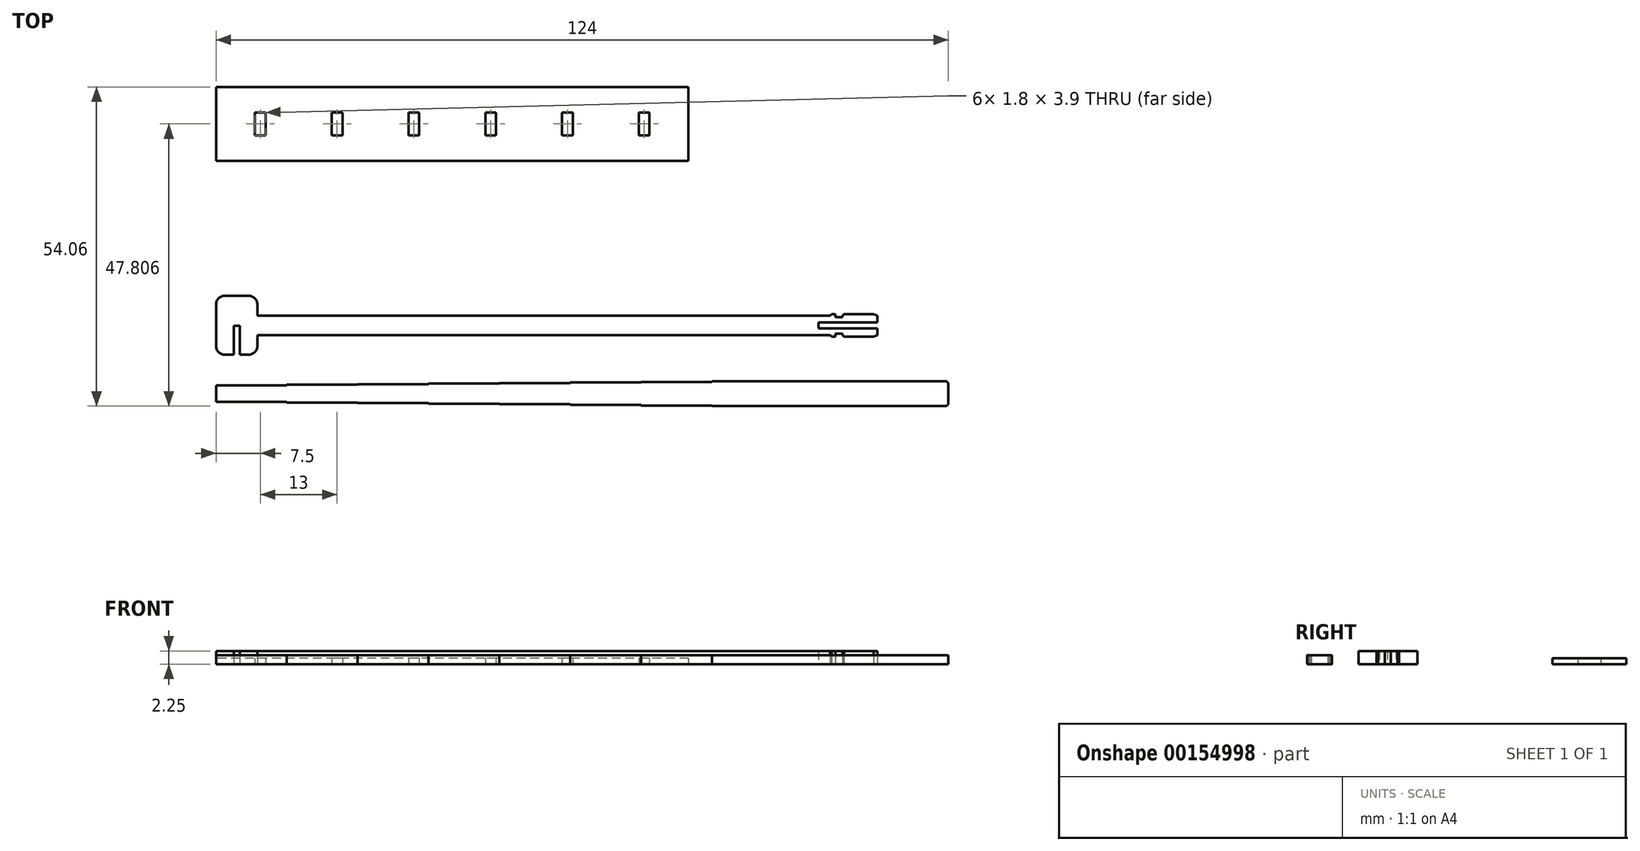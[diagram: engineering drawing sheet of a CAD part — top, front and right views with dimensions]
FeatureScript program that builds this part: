
annotation { "Feature Type Name" : "Feature", "Feature Type Description" : "" }
export const myFeature = defineFeature(function(context is Context, id is Id, definition is map)
    precondition{}
    {
        {
            var Q0;
            Q0=qCreatedBy(makeId("Top.planeOp"),FACE);
            var sketch = newSketch(context, id + "F0", { "sketchPlane" : qUnion([Q0])});
            skLineSegment(sketch, "E0", {"start": v(0, 0) * mm, "end": v(0, -1.4) * mm});
            skLineSegment(sketch, "E1", {"start": v(0, -1.4) * mm, "end": v(12, -1.4) * mm});
            skLineSegment(sketch, "E2", {"start": v(12, -1.4) * mm, "end": v(12, -1.5) * mm});
            skLineSegment(sketch, "E3", {"start": v(12, -1.5) * mm, "end": v(24, -1.5) * mm});
            skLineSegment(sketch, "E4", {"start": v(24, -1.5) * mm, "end": v(24, -1.6) * mm});
            skLineSegment(sketch, "E5", {"start": v(24, -1.6) * mm, "end": v(36, -1.6) * mm});
            skLineSegment(sketch, "E6", {"start": v(36, -1.6) * mm, "end": v(36, -1.7) * mm});
            skLineSegment(sketch, "E7", {"start": v(36, -1.7) * mm, "end": v(48, -1.7) * mm});
            skLineSegment(sketch, "E8", {"start": v(48, -1.7) * mm, "end": v(48, -1.8) * mm});
            skLineSegment(sketch, "E9", {"start": v(48, -1.8) * mm, "end": v(60, -1.8) * mm});
            skLineSegment(sketch, "E10", {"start": v(60, -1.8) * mm, "end": v(60, -1.9) * mm});
            skLineSegment(sketch, "E11", {"start": v(60, -1.9) * mm, "end": v(72, -1.9) * mm});
            skLineSegment(sketch, "E12", {"start": v(72, -1.9) * mm, "end": v(72, -2) * mm});
            skLineSegment(sketch, "E13", {"start": v(72, -2) * mm, "end": v(84, -2) * mm});
            skLineSegment(sketch, "E14", {"start": v(84, -2) * mm, "end": v(84, -2.1) * mm});
            skLineSegment(sketch, "E15", {"start": v(84, -2.1) * mm, "end": v(123.5, -2.1) * mm});
            skLineSegment(sketch, "E16", {"start": v(124, -1.6) * mm, "end": v(124, 0) * mm});
            skLineSegment(sketch, "E17.0", {"start": v(86, -1.1) * mm, "end": v(123, -1.1) * mm});
            skLineSegment(sketch, "E17.2", {"start": v(73, -1) * mm, "end": v(85, -1) * mm});
            skLineSegment(sketch, "E17.3", {"start": v(73, -0.9) * mm, "end": v(73, -1) * mm});
            skLineSegment(sketch, "E17.4", {"start": v(62, -0.9) * mm, "end": v(73, -0.9) * mm});
            skLineSegment(sketch, "E17.5", {"start": v(123, -1.1) * mm, "end": v(123, -0.95) * mm});
            skLineSegment(sketch, "E17.7", {"start": v(49, -0.8) * mm, "end": v(61, -0.8) * mm});
            skLineSegment(sketch, "E17.12", {"start": v(4, -0.5) * mm, "end": v(25, -0.5) * mm});
            skLineSegment(sketch, "E17.13", {"start": v(25, -0.5) * mm, "end": v(25, -0.6) * mm});
            skLineSegment(sketch, "E17.14", {"start": v(16, -0.6) * mm, "end": v(25, -0.6) * mm});
            skLineSegment(sketch, "E17.16", {"start": v(17, -0.7) * mm, "end": v(49, -0.7) * mm});
            skLineSegment(sketch, "E17.17", {"start": v(49, -0.7) * mm, "end": v(49, -0.8) * mm});
            skLineSegment(sketch, "E18", {"start": v(123, -0.95) * mm, "end": v(123, -0.45) * mm});
            skLineSegment(sketch, "E19.MirrorCS", {"start": v(84, 2) * mm, "end": v(84, 2.1) * mm});
            skLineSegment(sketch, "E20.MirrorCS", {"start": v(12, 1.4) * mm, "end": v(12, 1.5) * mm});
            skLineSegment(sketch, "E21.MirrorCS", {"start": v(24, 1.5) * mm, "end": v(24, 1.6) * mm});
            skLineSegment(sketch, "E22.MirrorCS", {"start": v(123, 0.95) * mm, "end": v(123, 0.45) * mm});
            skLineSegment(sketch, "E23.MirrorCS", {"start": v(48, 1.7) * mm, "end": v(48, 1.8) * mm});
            skLineSegment(sketch, "E24.MirrorCS", {"start": v(49, 0.7) * mm, "end": v(49, 0.8) * mm});
            skLineSegment(sketch, "E25.MirrorCS", {"start": v(73, 0.9) * mm, "end": v(73, 1) * mm});
            skLineSegment(sketch, "E26.MirrorCS", {"start": v(72, 1.9) * mm, "end": v(72, 2) * mm});
            skLineSegment(sketch, "E27.MirrorCS", {"start": v(60, 1.8) * mm, "end": v(60, 1.9) * mm});
            skLineSegment(sketch, "E28.MirrorCS", {"start": v(25, 0.5) * mm, "end": v(25, 0.6) * mm});
            skLineSegment(sketch, "E29.MirrorCS", {"start": v(36, 1.6) * mm, "end": v(36, 1.7) * mm});
            skLineSegment(sketch, "E30.MirrorCS", {"start": v(84, 2.1) * mm, "end": v(123.5, 2.1) * mm});
            skLineSegment(sketch, "E31.MirrorCS", {"start": v(0, 0) * mm, "end": v(0, 1.4) * mm});
            skLineSegment(sketch, "E32.MirrorCS", {"start": v(0, 1.4) * mm, "end": v(12, 1.4) * mm});
            skLineSegment(sketch, "E33.MirrorCS", {"start": v(12, 1.5) * mm, "end": v(24, 1.5) * mm});
            skLineSegment(sketch, "E34.MirrorCS", {"start": v(24, 1.6) * mm, "end": v(36, 1.6) * mm});
            skLineSegment(sketch, "E35.MirrorCS", {"start": v(86, 1.1) * mm, "end": v(123, 1.1) * mm});
            skLineSegment(sketch, "E36.MirrorCS", {"start": v(124, 1.6) * mm, "end": v(124, 0) * mm});
            skLineSegment(sketch, "E37.MirrorCS", {"start": v(48, 1.8) * mm, "end": v(60, 1.8) * mm});
            skLineSegment(sketch, "E38.MirrorCS", {"start": v(60, 1.9) * mm, "end": v(72, 1.9) * mm});
            skLineSegment(sketch, "E39.MirrorCS", {"start": v(4, 0.5) * mm, "end": v(25, 0.5) * mm});
            skLineSegment(sketch, "E40.MirrorCS", {"start": v(16, 0.6) * mm, "end": v(25, 0.6) * mm});
            skLineSegment(sketch, "E41.MirrorCS", {"start": v(17, 0.7) * mm, "end": v(49, 0.7) * mm});
            skLineSegment(sketch, "E42.MirrorCS", {"start": v(62, 0.9) * mm, "end": v(73, 0.9) * mm});
            skLineSegment(sketch, "E43.MirrorCS", {"start": v(49, 0.8) * mm, "end": v(61, 0.8) * mm});
            skLineSegment(sketch, "E44.MirrorCS", {"start": v(72, 2) * mm, "end": v(84, 2) * mm});
            skLineSegment(sketch, "E45.MirrorCS", {"start": v(73, 1) * mm, "end": v(85, 1) * mm});
            skLineSegment(sketch, "E46.MirrorCS", {"start": v(36, 1.7) * mm, "end": v(48, 1.7) * mm});
            skLineSegment(sketch, "E47.MirrorCS", {"start": v(123, 1.1) * mm, "end": v(123, 0.95) * mm});
            skLineSegment(sketch, "E48", {"start": v(16, 0.6) * mm, "end": v(16, -0.6) * mm});
            skLineSegment(sketch, "E49", {"start": v(17, -0.7) * mm, "end": v(17, 0.7) * mm});
            skLineSegment(sketch, "E50", {"start": v(61, -0.8) * mm, "end": v(61, 0.8) * mm});
            skLineSegment(sketch, "E51", {"start": v(86, -1.1) * mm, "end": v(86, 1.1) * mm});
            skPoint(sketch, "E52.orphan", {"position": v(37, -0.7) * mm});
            skPoint(sketch, "E53.orphan", {"position": v(61, -0.9) * mm});
            skPoint(sketch, "E54.orphan", {"position": v(85, -1.1) * mm});
            skPoint(sketch, "E55.MirrorCS.end.orphan", {"position": v(85, 1.1) * mm});
            skPoint(sketch, "E56.MirrorCS.end.orphan", {"position": v(61, 0.9) * mm});
            skPoint(sketch, "E57.MirrorCS.end.orphan", {"position": v(37, 0.7) * mm});
            skLineSegment(sketch, "E58.trimOffspring", {"start": v(62, 0.9) * mm, "end": v(62, -0.9) * mm});
            skLineSegment(sketch, "E59", {"start": v(4, -0.5) * mm, "end": v(4, 0.5) * mm});
            skLineSegment(sketch, "E60", {"start": v(123, -0.45) * mm, "end": v(123, 0.45) * mm});
            skLineSegment(sketch, "E61.trimOffspring", {"start": v(85, 1) * mm, "end": v(85, -1) * mm});
            skPoint(sketch, "E62.visualSharp", {"position": v(124, -2.1) * mm});
            skArc(sketch, "E62.filletArc", {"start": v(123.5, -2.1) * mm, "mid": v(123.85, -1.95) * mm, "end": v(124, -1.6) * mm});
            skPoint(sketch, "E63.visualSharp", {"position": v(124, 2.1) * mm});
            skArc(sketch, "E63.filletArc", {"start": v(124, 1.6) * mm, "mid": v(123.85, 1.95) * mm, "end": v(123.5, 2.1) * mm});
            skLineSegment(sketch, "E64", {"start": v(0, 8.08) * mm, "end": v(0, 11.58) * mm});
            skPoint(sketch, "E64.startSnap0", {"position": v(0, 0.7) * mm});
            skLineSegment(sketch, "E65", {"start": v(0, 11.58) * mm, "end": v(102, 11.58) * mm});
            skLineSegment(sketch, "E66", {"start": v(112, 11.08) * mm, "end": v(112, 9.93) * mm});
            skLineSegment(sketch, "E67", {"start": v(5.5, 6.58) * mm, "end": v(4, 6.58) * mm});
            skLineSegment(sketch, "E68", {"start": v(7, 9.93) * mm, "end": v(104, 9.93) * mm});
            skLineSegment(sketch, "E69", {"start": v(7, 9.93) * mm, "end": v(7, 8.08) * mm});
            skLineSegment(sketch, "E70", {"start": v(111.31, 9.68) * mm, "end": v(106.32, 9.68) * mm});
            skPoint(sketch, "E71.orphan", {"position": v(112, 6.58) * mm});
            skLineSegment(sketch, "E72", {"start": v(112, 11.08) * mm, "end": v(102, 11.08) * mm});
            skLineSegment(sketch, "E73", {"start": v(102, 11.08) * mm, "end": v(102, 11.58) * mm});
            skLineSegment(sketch, "E74.MirrorCS", {"start": v(7, 13.23) * mm, "end": v(7, 15.08) * mm});
            skLineSegment(sketch, "E75.MirrorCS", {"start": v(5.5, 16.58) * mm, "end": v(1.5, 16.58) * mm});
            skLineSegment(sketch, "E76.MirrorCS", {"start": v(0, 15.08) * mm, "end": v(0, 11.58) * mm});
            skLineSegment(sketch, "E77.MirrorCS", {"start": v(7, 13.23) * mm, "end": v(104, 13.23) * mm});
            skLineSegment(sketch, "E78.MirrorCS", {"start": v(102, 12.08) * mm, "end": v(102, 11.58) * mm});
            skLineSegment(sketch, "E79.MirrorCS", {"start": v(111.31, 13.48) * mm, "end": v(106.32, 13.48) * mm});
            skLineSegment(sketch, "E80.MirrorCS", {"start": v(112, 12.08) * mm, "end": v(112, 13.23) * mm});
            skLineSegment(sketch, "E81.MirrorCS", {"start": v(112, 12.08) * mm, "end": v(102, 12.08) * mm});
            skPoint(sketch, "E82.MirrorP", {"position": v(112, 16.58) * mm});
            skPoint(sketch, "E83.orphan", {"position": v(112, 11.58) * mm});
            skPoint(sketch, "E84.orphan", {"position": v(112, 13.23) * mm});
            skPoint(sketch, "E85.orphan", {"position": v(112, 9.93) * mm});
            skPoint(sketch, "E86.visualSharp", {"position": v(0, 6.58) * mm});
            skArc(sketch, "E86.filletArc", {"start": v(0, 8.08) * mm, "mid": v(0.44, 7.02) * mm, "end": v(1.5, 6.58) * mm});
            skPoint(sketch, "E87.visualSharp", {"position": v(0, 16.58) * mm});
            skArc(sketch, "E87.filletArc", {"start": v(1.5, 16.58) * mm, "mid": v(0.44, 16.14) * mm, "end": v(0, 15.08) * mm});
            skPoint(sketch, "E88.visualSharp", {"position": v(7, 6.58) * mm});
            skArc(sketch, "E88.filletArc", {"start": v(5.5, 6.58) * mm, "mid": v(6.56, 7.02) * mm, "end": v(7, 8.08) * mm});
            skPoint(sketch, "E89.visualSharp", {"position": v(7, 16.58) * mm});
            skArc(sketch, "E89.filletArc", {"start": v(7, 15.08) * mm, "mid": v(6.56, 16.14) * mm, "end": v(5.5, 16.58) * mm});
            skLineSegment(sketch, "E90", {"start": v(104, 9.93) * mm, "end": v(104.25, 9.68) * mm});
            skLineSegment(sketch, "E91.MirrorCS", {"start": v(104, 13.23) * mm, "end": v(104.25, 13.48) * mm});
            skLineSegment(sketch, "E92", {"start": v(112, 9.93) * mm, "end": v(111.31, 9.68) * mm});
            skLineSegment(sketch, "E93.MirrorCS", {"start": v(112, 13.23) * mm, "end": v(111.31, 13.48) * mm});
            skPoint(sketch, "E94.orphan", {"position": v(104, 9.68) * mm});
            skPoint(sketch, "E95.orphan", {"position": v(104, 13.48) * mm});
            skPoint(sketch, "E96.orphan", {"position": v(112, 9.68) * mm});
            skPoint(sketch, "E97.orphan", {"position": v(112, 13.48) * mm});
            skLineSegment(sketch, "E98", {"start": v(3, 6.58) * mm, "end": v(3, 11.48) * mm});
            skLineSegment(sketch, "E99", {"start": v(3, 11.48) * mm, "end": v(4, 11.48) * mm});
            skLineSegment(sketch, "E100", {"start": v(4, 11.48) * mm, "end": v(4, 6.58) * mm});
            skLineSegment(sketch, "E101.trimOffspring", {"start": v(3, 6.58) * mm, "end": v(1.5, 6.58) * mm});
            skLineSegment(sketch, "E102", {"start": v(107.78, 9.68) * mm, "end": v(107.78, 13.48) * mm, "construction": true});
            skLineSegment(sketch, "E103", {"start": v(104.87, 9.68) * mm, "end": v(104.87, 9.93) * mm});
            skLineSegment(sketch, "E104.0", {"start": v(106.07, 9.68) * mm, "end": v(106.07, 9.93) * mm});
            skLineSegment(sketch, "E105", {"start": v(106.07, 9.93) * mm, "end": v(106.32, 9.68) * mm});
            skLineSegment(sketch, "E106.trimOffspring", {"start": v(104.87, 9.68) * mm, "end": v(104.25, 9.68) * mm});
            skLineSegment(sketch, "E107.MirrorCS", {"start": v(104.87, 13.48) * mm, "end": v(104.87, 13.24) * mm});
            skLineSegment(sketch, "E108.MirrorCS", {"start": v(106.07, 13.24) * mm, "end": v(106.32, 13.48) * mm});
            skLineSegment(sketch, "E109.trimOffspring", {"start": v(104.87, 13.48) * mm, "end": v(104.25, 13.48) * mm});
            skPoint(sketch, "E110.MirrorCS.start.orphan", {"position": v(106.07, 13.48) * mm});
            skLineSegment(sketch, "E111", {"start": v(104.87, 9.93) * mm, "end": v(104.87, 10.18) * mm});
            skLineSegment(sketch, "E112", {"start": v(104.87, 10.18) * mm, "end": v(106.07, 10.18) * mm});
            skLineSegment(sketch, "E113", {"start": v(106.07, 10.18) * mm, "end": v(106.07, 9.93) * mm});
            skLineSegment(sketch, "E114.MirrorCS", {"start": v(104.87, 13.24) * mm, "end": v(104.87, 12.99) * mm});
            skLineSegment(sketch, "E115.MirrorCS", {"start": v(104.87, 12.99) * mm, "end": v(106.07, 12.99) * mm});
            skLineSegment(sketch, "E116.MirrorCS", {"start": v(106.07, 12.99) * mm, "end": v(106.07, 13.24) * mm});
            skSolve(sketch);
        }
        {
            var Q0;
            Q0=makeQuery(id+"F0.imprint","IMPRINT",FACE,{"disambiguationData":[TD([[makeQuery(id+"F0.imprint","IMPRINT",EDGE,{"derivedFrom":sQuery(id+"F0.wireOp",EDGE,"E0")}),1.0]])]});
            var Q1;
            {var subQ0=sQuery(id+"F0.wireOp",EDGE,"E48");var subQ1=sQuery(id+"F0.wireOp",EDGE,"E17.12");var subQ2=makeQuery(id+"F0.imprint","INTERSECT",VERTEX,{"derivedFrom":[subQ1,subQ0]});Q1=makeQuery(id+"F0.imprint","IMPRINT",FACE,{"disambiguationData":[TD([[makeQuery(id+"F0.imprint","IMPRINT",EDGE,{"disambiguationData":[TD([[subQ2,-1.0]])],"derivedFrom":subQ1}),1.0]])]});}
            var Q2;
            {var subQ0=sQuery(id+"F0.wireOp",EDGE,"E59");Q2=makeQuery(id+"F0.imprint","IMPRINT",FACE,{"disambiguationData":[TD([[makeQuery(id+"F0.imprint","IMPRINT",EDGE,{"derivedFrom":subQ0}),-1.0]])]});}
            var Q3;
            Q3=makeQuery(id+"F0.imprint","IMPRINT",FACE,{"disambiguationData":[TD([[makeQuery(id+"F0.imprint","IMPRINT",EDGE,{"derivedFrom":sQuery(id+"F0.wireOp",EDGE,"E64")}),-1.0]])]});
            var Q4;
            {var subQ0=sQuery(id+"F0.wireOp",EDGE,"E28.MirrorCS");Q4=makeQuery(id+"F0.imprint","IMPRINT",FACE,{"disambiguationData":[TD([[makeQuery(id+"F0.imprint","IMPRINT",EDGE,{"derivedFrom":subQ0}),1.0]])]});}
            var Q5;
            {var subQ0=sQuery(id+"F0.wireOp",EDGE,"E17.13");Q5=makeQuery(id+"F0.imprint","IMPRINT",FACE,{"disambiguationData":[TD([[makeQuery(id+"F0.imprint","IMPRINT",EDGE,{"derivedFrom":subQ0}),-1.0]])]});}
            var Q6;
            {var subQ0=sQuery(id+"F0.wireOp",EDGE,"E48");var subQ1=sQuery(id+"F0.wireOp",EDGE,"E17.12");var subQ2=makeQuery(id+"F0.imprint","INTERSECT",VERTEX,{"derivedFrom":[subQ1,subQ0]});Q6=makeQuery(id+"F0.imprint","IMPRINT",FACE,{"disambiguationData":[TD([[makeQuery(id+"F0.imprint","IMPRINT",EDGE,{"disambiguationData":[TD([[subQ2,-1.0]])],"derivedFrom":subQ1}),-1.0]])]});}
            var Q7;
            {var subQ0=sQuery(id+"F0.wireOp",EDGE,"E48");var subQ1=sQuery(id+"F0.wireOp",EDGE,"E39.MirrorCS");var subQ2=makeQuery(id+"F0.imprint","INTERSECT",VERTEX,{"derivedFrom":[subQ1,subQ0]});Q7=makeQuery(id+"F0.imprint","IMPRINT",FACE,{"disambiguationData":[TD([[makeQuery(id+"F0.imprint","IMPRINT",EDGE,{"disambiguationData":[TD([[subQ2,-1.0]])],"derivedFrom":subQ1}),1.0]])]});}
            var Q8;
            Q8=makeQuery(id+"F0.imprint","IMPRINT",FACE,{"disambiguationData":[TD([[makeQuery(id+"F0.imprint","IMPRINT",EDGE,{"derivedFrom":sQuery(id+"F0.wireOp",EDGE,"E17.7")}),1.0]])]});
            var Q9;
            Q9=makeQuery(id+"F0.imprint","IMPRINT",FACE,{"disambiguationData":[TD([[makeQuery(id+"F0.imprint","IMPRINT",EDGE,{"derivedFrom":sQuery(id+"F0.wireOp",EDGE,"E17.0")}),1.0]])]});
            var Q10;
            Q10=makeQuery(id+"F0.imprint","IMPRINT",FACE,{"disambiguationData":[TD([[makeQuery(id+"F0.imprint","IMPRINT",EDGE,{"derivedFrom":sQuery(id+"F0.wireOp",EDGE,"E17.2")}),1.0]])]});
            extrude(context, id + "F1", {"entities" : qUnion([Q0, Q1, Q2, Q3, Q4, Q5, Q6, Q7, Q8, Q9, Q10]), "depth" : 1.5 * mm});
        }
        {
            var Q0;
            Q0=makeQuery(id+"F0.imprint","IMPRINT",FACE,{"disambiguationData":[TD([[makeQuery(id+"F0.imprint","IMPRINT",EDGE,{"derivedFrom":sQuery(id+"F0.wireOp",EDGE,"E65")}),1.0]])]});
            var Q1;
            Q1=makeQuery(id+"F0.imprint","IMPRINT",FACE,{"disambiguationData":[TD([[makeQuery(id+"F0.imprint","IMPRINT",EDGE,{"derivedFrom":sQuery(id+"F0.wireOp",EDGE,"E64")}),-1.0]])]});
            extrude(context, id + "F2", {"entities" : qUnion([Q0, Q1]), "operationType" : NewBodyOperationType.ADD, "depth" : 2.25 * mm});
        }
        {
            var Q0;
            Q0=qCreatedBy(makeId("Top.planeOp"),FACE);
            var sketch = newSketch(context, id + "F3", { "sketchPlane" : qUnion([Q0])});
            skLineSegment(sketch, "E117", {"start": v(0, 51.96) * mm, "end": v(0, 39.46) * mm});
            skLineSegment(sketch, "E118", {"start": v(0, 39.46) * mm, "end": v(80, 39.46) * mm});
            skLineSegment(sketch, "E119", {"start": v(80, 39.46) * mm, "end": v(80, 51.96) * mm});
            skLineSegment(sketch, "E120", {"start": v(80, 51.96) * mm, "end": v(0, 51.96) * mm});
            skLineSegment(sketch, "E121.2.0.0", {"start": v(90, 39.46) * mm, "end": v(90, 54.46) * mm, "construction": true});
            skLineSegment(sketch, "E121.2.0.1", {"start": v(96.25, 39.46) * mm, "end": v(96.25, 54.46) * mm, "construction": true});
            skLineSegment(sketch, "E122", {"start": v(6.6, 43.76) * mm, "end": v(6.6, 47.66) * mm});
            skLineSegment(sketch, "E123", {"start": v(6.6, 47.66) * mm, "end": v(8.4, 47.66) * mm});
            skLineSegment(sketch, "E124", {"start": v(8.4, 47.66) * mm, "end": v(8.4, 43.76) * mm});
            skLineSegment(sketch, "E125", {"start": v(8.4, 43.76) * mm, "end": v(6.6, 43.76) * mm});
            skLineSegment(sketch, "E126", {"start": v(0, 45.7) * mm, "end": v(52.06, 45.7) * mm, "construction": true});
            skPoint(sketch, "E127", {"position": v(7.5, 43.76) * mm});
            skPoint(sketch, "E128", {"position": v(6.6, 45.7) * mm});
            skLineSegment(sketch, "E129.1.0.0", {"start": v(21.4, 43.76) * mm, "end": v(19.6, 43.76) * mm});
            skLineSegment(sketch, "E129.1.0.1", {"start": v(19.6, 43.76) * mm, "end": v(19.6, 47.66) * mm});
            skLineSegment(sketch, "E129.1.0.2", {"start": v(21.4, 47.66) * mm, "end": v(21.4, 43.76) * mm});
            skLineSegment(sketch, "E129.1.0.3", {"start": v(19.6, 47.66) * mm, "end": v(21.4, 47.66) * mm});
            skLineSegment(sketch, "E129.2.0.0", {"start": v(34.4, 43.76) * mm, "end": v(32.6, 43.76) * mm});
            skLineSegment(sketch, "E129.2.0.1", {"start": v(32.6, 43.76) * mm, "end": v(32.6, 47.66) * mm});
            skLineSegment(sketch, "E129.2.0.2", {"start": v(34.4, 47.66) * mm, "end": v(34.4, 43.76) * mm});
            skLineSegment(sketch, "E129.2.0.3", {"start": v(32.6, 47.66) * mm, "end": v(34.4, 47.66) * mm});
            skLineSegment(sketch, "E129.3.0.0", {"start": v(47.4, 43.76) * mm, "end": v(45.6, 43.76) * mm});
            skLineSegment(sketch, "E129.3.0.1", {"start": v(45.6, 43.76) * mm, "end": v(45.6, 47.66) * mm});
            skLineSegment(sketch, "E129.3.0.2", {"start": v(47.4, 47.66) * mm, "end": v(47.4, 43.76) * mm});
            skLineSegment(sketch, "E129.3.0.3", {"start": v(45.6, 47.66) * mm, "end": v(47.4, 47.66) * mm});
            skLineSegment(sketch, "E129.4.0.0", {"start": v(60.4, 43.76) * mm, "end": v(58.6, 43.76) * mm});
            skLineSegment(sketch, "E129.4.0.1", {"start": v(58.6, 43.76) * mm, "end": v(58.6, 47.66) * mm});
            skLineSegment(sketch, "E129.4.0.2", {"start": v(60.4, 47.66) * mm, "end": v(60.4, 43.76) * mm});
            skLineSegment(sketch, "E129.4.0.3", {"start": v(58.6, 47.66) * mm, "end": v(60.4, 47.66) * mm});
            skLineSegment(sketch, "E129.direction1", {"start": v(6.6, 43.76) * mm, "end": v(19.6, 43.76) * mm, "construction": true});
            skLineSegment(sketch, "E130", {"start": v(34.4, 43.76) * mm, "end": v(45.6, 43.76) * mm, "construction": true});
            skPoint(sketch, "E131", {"position": v(40, 43.76) * mm});
            skLineSegment(sketch, "E132", {"start": v(40, 39.46) * mm, "end": v(40, 51.96) * mm, "construction": true});
            skLineSegment(sketch, "E133.0.5.0", {"start": v(73.4, 43.76) * mm, "end": v(71.6, 43.76) * mm});
            skLineSegment(sketch, "E133.3.5.0", {"start": v(71.6, 43.76) * mm, "end": v(71.6, 47.66) * mm});
            skLineSegment(sketch, "E133.6.5.0", {"start": v(73.4, 47.66) * mm, "end": v(73.4, 43.76) * mm});
            skLineSegment(sketch, "E133.9.5.0", {"start": v(71.6, 47.66) * mm, "end": v(73.4, 47.66) * mm});
            skSolve(sketch);
        }
        {
            var Q0;
            Q0=makeQuery(id+"F3.imprint","IMPRINT",FACE,{"disambiguationData":[TD([[makeQuery(id+"F3.imprint","IMPRINT",EDGE,{"derivedFrom":sQuery(id+"F3.wireOp",EDGE,"E117")}),1.0]])]});
            extrude(context, id + "F4", {"entities" : qUnion([Q0]), "depth" : 1 * mm});
        }
    });
